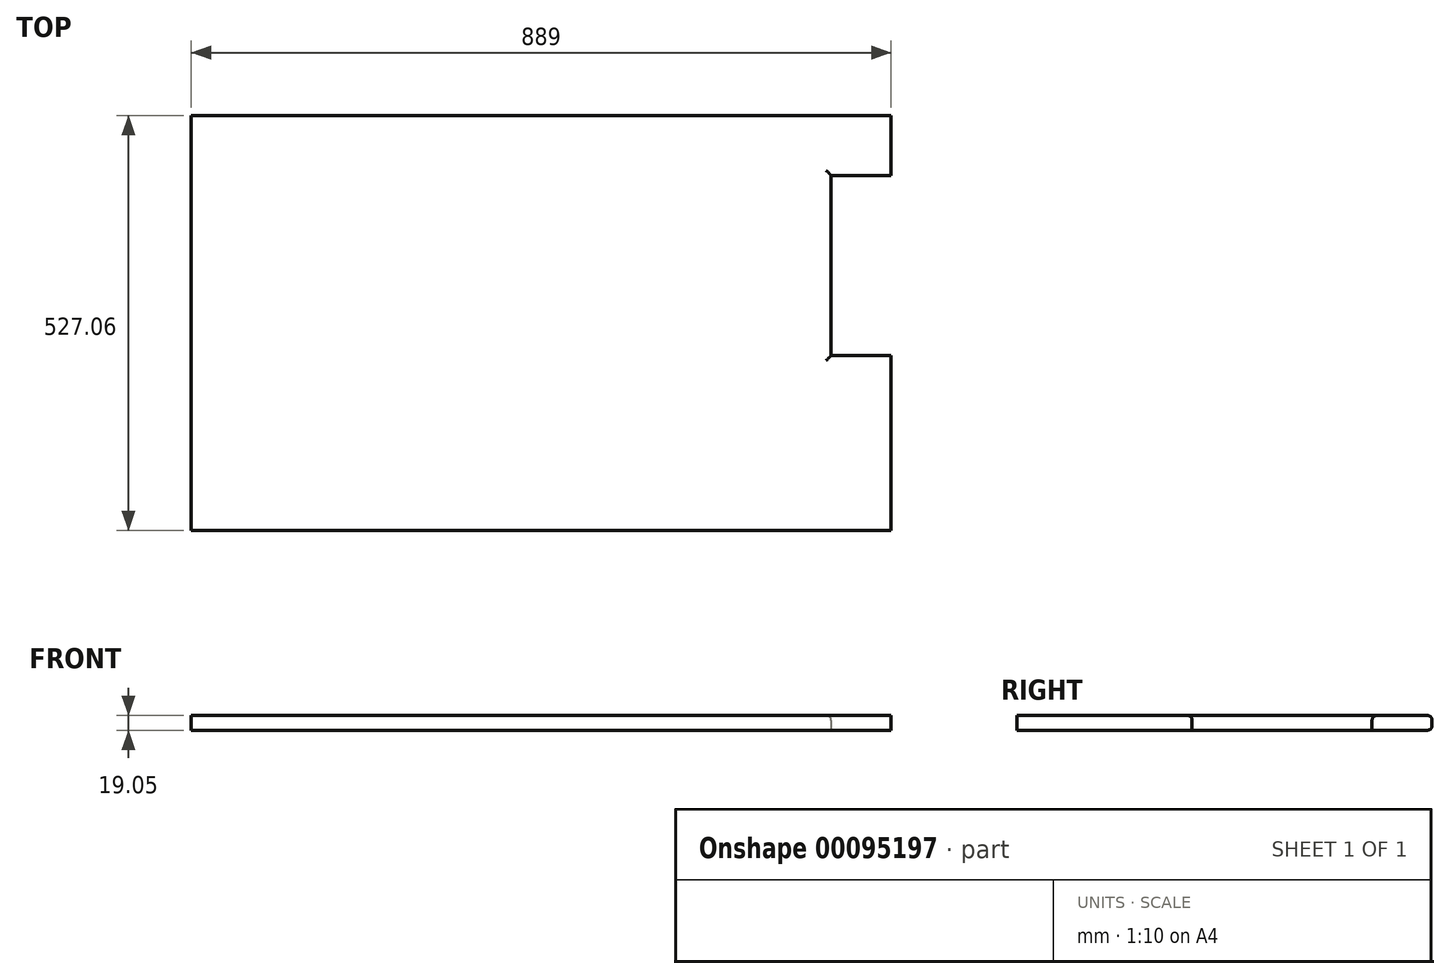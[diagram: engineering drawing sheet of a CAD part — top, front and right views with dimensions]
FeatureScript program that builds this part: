
annotation { "Feature Type Name" : "Feature", "Feature Type Description" : "" }
export const myFeature = defineFeature(function(context is Context, id is Id, definition is map)
    precondition{}
    {
        {
            var Q0;
            Q0=qCreatedBy(makeId("Top.planeOp"),FACE);
            var sketch = newSketch(context, id + "F0", { "sketchPlane" : qUnion([Q0])});
            skLineSegment(sketch, "E0.bottom", {"start": v(444.5, -263.52) * mm, "end": v(-444.5, -263.53) * mm});
            skLineSegment(sketch, "E0.top", {"start": v(444.5, 263.53) * mm, "end": v(-444.5, 263.53) * mm});
            skLineSegment(sketch, "E0.left", {"start": v(444.5, -263.52) * mm, "end": v(444.5, 263.53) * mm});
            skLineSegment(sketch, "E0.right", {"start": v(-444.5, -263.53) * mm, "end": v(-444.5, 263.53) * mm});
            skPoint(sketch, "E0.middle", {"position": v(0, 0) * mm});
            skLineSegment(sketch, "E1.bottom", {"start": v(444.5, 187.33) * mm, "end": v(368.3, 187.33) * mm});
            skLineSegment(sketch, "E1.top", {"start": v(444.5, -41.27) * mm, "end": v(368.3, -41.27) * mm});
            skLineSegment(sketch, "E1.left", {"start": v(444.5, 187.33) * mm, "end": v(444.5, -41.27) * mm});
            skLineSegment(sketch, "E1.right", {"start": v(368.3, 187.33) * mm, "end": v(368.3, -41.27) * mm});
            skLineSegment(sketch, "E2", {"start": v(444.5, 263.53) * mm, "end": v(444.5, 187.33) * mm, "construction": true});
            skSolve(sketch);
        }
        {
            var Q0;
            Q0=makeQuery(id+"F0.imprint","IMPRINT",FACE,{"disambiguationData":[TD([[makeQuery(id+"F0.imprint","IMPRINT",EDGE,{"derivedFrom":sQuery(id+"F0.wireOp",EDGE,"E0.bottom")}),-1.0]])]});
            extrude(context, id + "F1", {"entities" : qUnion([Q0]), "depth" : 19.05 * mm});
        }
        {
            var Q0;
            Q0=makeQuery(id+"F1.opExtrude","CAP_EDGE",EDGE,{"disambiguationData":[OSD([sQuery(id+"F0.wireOp",EDGE,"E0.top")])],"isStart":false});
            var Q1;
            Q1=makeQuery(id+"F1.opExtrude","CAP_EDGE",EDGE,{"disambiguationData":[OSD([sQuery(id+"F0.wireOp",EDGE,"E0.top")])],"isStart":true});
            var Q2;
            Q2=makeQuery(id+"F1.opExtrude","CAP_EDGE",EDGE,{"disambiguationData":[OSD([sQuery(id+"F0.wireOp",EDGE,"E1.top")])],"isStart":false});
            var Q3;
            Q3=makeQuery(id+"F1.opExtrude","CAP_EDGE",EDGE,{"disambiguationData":[OSD([sQuery(id+"F0.wireOp",EDGE,"E1.right")])],"isStart":false});
            var Q4;
            Q4=makeQuery(id+"F1.opExtrude","CAP_EDGE",EDGE,{"disambiguationData":[OSD([sQuery(id+"F0.wireOp",EDGE,"E1.bottom")])],"isStart":false});
            fillet(context, id + "F2", {"entities" : qUnion([Q0, Q1, Q2, Q3, Q4]), "radius" : 6.35 * mm, "tangentPropagation" : true, "allowEdgeOverflow" : false});
        }
    });
